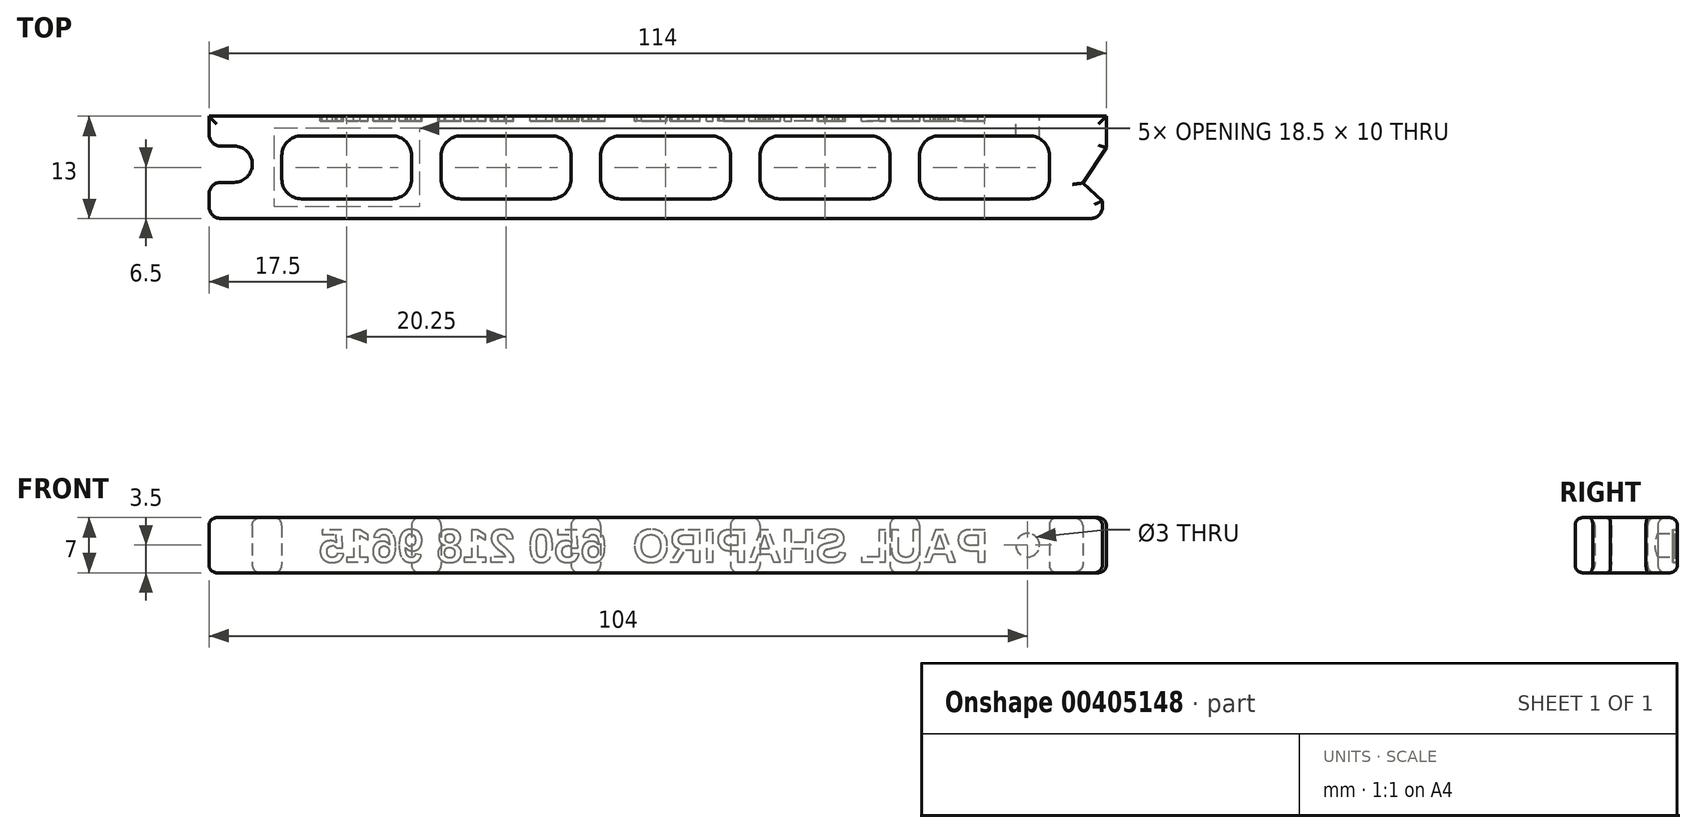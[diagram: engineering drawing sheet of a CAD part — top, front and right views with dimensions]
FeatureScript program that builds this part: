
annotation { "Feature Type Name" : "Feature", "Feature Type Description" : "" }
export const myFeature = defineFeature(function(context is Context, id is Id, definition is map)
    precondition{}
    {
        {
            var Q0;
            Q0=qCreatedBy(makeId("Top.planeOp"),FACE);
            var sketch = newSketch(context, id + "F0", { "sketchPlane" : qUnion([Q0])});
            skLineSegment(sketch, "E0.bottom", {"start": v(1.5, 0) * mm, "end": v(112, 0) * mm});
            skLineSegment(sketch, "E0.top", {"start": v(0, 13) * mm, "end": v(114, 13) * mm});
            skLineSegment(sketch, "E1", {"start": v(0, 13) * mm, "end": v(0, 10.7) * mm});
            skLineSegment(sketch, "E2.bottom", {"start": v(1.5, 4.6) * mm, "end": v(3.2, 4.6) * mm});
            skLineSegment(sketch, "E2.top", {"start": v(1.5, 9.2) * mm, "end": v(3.2, 9.2) * mm});
            skArc(sketch, "E3", {"start": v(3.2, 4.6) * mm, "mid": v(5.5, 6.9) * mm, "end": v(3.2, 9.2) * mm});
            skLineSegment(sketch, "E4.trimOffspring", {"start": v(0, 3.1) * mm, "end": v(0, 1.5) * mm});
            skLineSegment(sketch, "E5", {"start": v(0, 9.2) * mm, "end": v(0, 4.6) * mm, "construction": true});
            skLineSegment(sketch, "E6", {"start": v(0, 6.9) * mm, "end": v(3.2, 6.9) * mm, "construction": true});
            skLineSegment(sketch, "E7", {"start": v(114, 13) * mm, "end": v(114, 9) * mm});
            skPoint(sketch, "E8.visualSharp", {"position": v(0, 0) * mm});
            skArc(sketch, "E8.filletArc", {"start": v(0, 1.5) * mm, "mid": v(0.44, 0.44) * mm, "end": v(1.5, 0) * mm});
            skPoint(sketch, "E9.visualSharp", {"position": v(0, 4.6) * mm});
            skArc(sketch, "E9.filletArc", {"start": v(1.5, 4.6) * mm, "mid": v(0.44, 4.16) * mm, "end": v(0, 3.1) * mm});
            skPoint(sketch, "E10.visualSharp", {"position": v(0, 9.2) * mm});
            skArc(sketch, "E10.filletArc", {"start": v(0, 10.7) * mm, "mid": v(0.44, 9.64) * mm, "end": v(1.5, 9.2) * mm});
            skPoint(sketch, "E11.visualSharp", {"position": v(114, 4.5) * mm});
            skLineSegment(sketch, "E12", {"start": v(114, 4.5) * mm, "end": v(111, 4.5) * mm, "construction": true});
            skLineSegment(sketch, "E13", {"start": v(114, 9) * mm, "end": v(111, 4.5) * mm});
            skLineSegment(sketch, "E14", {"start": v(113.5, 2.25) * mm, "end": v(111, 4.5) * mm});
            skArc(sketch, "E15", {"start": v(112, 0) * mm, "mid": v(113.06, 0.44) * mm, "end": v(113.5, 1.5) * mm});
            skLineSegment(sketch, "E16", {"start": v(112, 1.5) * mm, "end": v(114.8, 1.5) * mm, "construction": true});
            skLineSegment(sketch, "E17", {"start": v(113.5, 2.25) * mm, "end": v(113.5, 1.5) * mm});
            skSolve(sketch);
        }
        {
            var Q0;
            Q0=makeQuery(id+"F0.imprint","IMPRINT",FACE,{"disambiguationData":[TD([[makeQuery(id+"F0.imprint","IMPRINT",EDGE,{"derivedFrom":sQuery(id+"F0.wireOp",EDGE,"E0.bottom")}),1.0]])]});
            extrude(context, id + "F1", {"entities" : qUnion([Q0]), "depth" : 7 * mm});
        }
        {
            var Q0;
            Q0=makeQuery(id+"F1.opExtrude","CAP_FACE",FACE,{"disambiguationData":[OSD([sQuery(id+"F0.wireOp",EDGE,"E0.bottom"),sQuery(id+"F0.wireOp",EDGE,"E0.top"),sQuery(id+"F0.wireOp",EDGE,"E1"),sQuery(id+"F0.wireOp",EDGE,"E2.bottom"),sQuery(id+"F0.wireOp",EDGE,"E2.top"),sQuery(id+"F0.wireOp",EDGE,"E3"),sQuery(id+"F0.wireOp",EDGE,"E4.trimOffspring"),sQuery(id+"F0.wireOp",EDGE,"E7"),sQuery(id+"F0.wireOp",EDGE,"c30ca287-96d4-4dfe-8688-3bdeec023004"),sQuery(id+"F0.wireOp",EDGE,"f645941c-dc99-4dda-a8e2-c4b280260802"),sQuery(id+"F0.wireOp",EDGE,"a89c6d0d-95b4-4aa5-8d05-a083aa38cfd4")])],"isStart":true});
            var sketch = newSketch(context, id + "F2", { "sketchPlane" : qUnion([Q0])});
            skLineSegment(sketch, "E18.bottom", {"start": v(104.25, -2.5) * mm, "end": v(92.75, -2.5) * mm});
            skLineSegment(sketch, "E18.top", {"start": v(104.25, -10.5) * mm, "end": v(92.75, -10.5) * mm});
            skLineSegment(sketch, "E18.left", {"start": v(106.75, -5) * mm, "end": v(106.75, -8) * mm});
            skLineSegment(sketch, "E18.right", {"start": v(90.25, -5) * mm, "end": v(90.25, -8) * mm});
            skLineSegment(sketch, "E19", {"start": v(106.75, -10.5) * mm, "end": v(106.75, -13) * mm, "construction": true});
            skLineSegment(sketch, "E20", {"start": v(106.75, -2.5) * mm, "end": v(106.75, 0) * mm, "construction": true});
            skPoint(sketch, "E21.visualSharp", {"position": v(90.25, -10.5) * mm});
            skArc(sketch, "E21.filletArc", {"start": v(90.25, -8) * mm, "mid": v(90.98, -9.77) * mm, "end": v(92.75, -10.5) * mm});
            skPoint(sketch, "E22.visualSharp", {"position": v(90.25, -2.5) * mm});
            skArc(sketch, "E22.filletArc", {"start": v(92.75, -2.5) * mm, "mid": v(90.98, -3.23) * mm, "end": v(90.25, -5) * mm});
            skPoint(sketch, "E23.visualSharp", {"position": v(106.75, -2.5) * mm});
            skArc(sketch, "E23.filletArc", {"start": v(106.75, -5) * mm, "mid": v(106.02, -3.23) * mm, "end": v(104.25, -2.5) * mm});
            skPoint(sketch, "E24.visualSharp", {"position": v(106.75, -10.5) * mm});
            skArc(sketch, "E24.filletArc", {"start": v(104.25, -10.5) * mm, "mid": v(106.02, -9.77) * mm, "end": v(106.75, -8) * mm});
            skLineSegment(sketch, "E25.1.0.0", {"start": v(84, -2.5) * mm, "end": v(72.5, -2.5) * mm});
            skPoint(sketch, "E25.1.0.1", {"position": v(86.5, -2.5) * mm});
            skLineSegment(sketch, "E25.1.0.2", {"start": v(84, -10.5) * mm, "end": v(72.5, -10.5) * mm});
            skPoint(sketch, "E25.1.0.3", {"position": v(86.5, -10.5) * mm});
            skLineSegment(sketch, "E25.1.0.4", {"start": v(70, -5) * mm, "end": v(70, -8) * mm});
            skLineSegment(sketch, "E25.1.0.5", {"start": v(86.5, -5) * mm, "end": v(86.5, -8) * mm});
            skPoint(sketch, "E25.1.0.6", {"position": v(70, -2.5) * mm});
            skPoint(sketch, "E25.1.0.7", {"position": v(70, -10.5) * mm});
            skArc(sketch, "E25.1.0.8", {"start": v(72.5, -2.5) * mm, "mid": v(70.73, -3.23) * mm, "end": v(70, -5) * mm});
            skArc(sketch, "E25.1.0.9", {"start": v(70, -8) * mm, "mid": v(70.73, -9.77) * mm, "end": v(72.5, -10.5) * mm});
            skArc(sketch, "E25.1.0.10", {"start": v(86.5, -5) * mm, "mid": v(85.77, -3.23) * mm, "end": v(84, -2.5) * mm});
            skArc(sketch, "E25.1.0.11", {"start": v(84, -10.5) * mm, "mid": v(85.77, -9.77) * mm, "end": v(86.5, -8) * mm});
            skLineSegment(sketch, "E25.2.0.0", {"start": v(63.75, -2.5) * mm, "end": v(52.25, -2.5) * mm});
            skPoint(sketch, "E25.2.0.1", {"position": v(66.25, -2.5) * mm});
            skLineSegment(sketch, "E25.2.0.2", {"start": v(63.75, -10.5) * mm, "end": v(52.25, -10.5) * mm});
            skPoint(sketch, "E25.2.0.3", {"position": v(66.25, -10.5) * mm});
            skLineSegment(sketch, "E25.2.0.4", {"start": v(49.75, -5) * mm, "end": v(49.75, -8) * mm});
            skLineSegment(sketch, "E25.2.0.5", {"start": v(66.25, -5) * mm, "end": v(66.25, -8) * mm});
            skPoint(sketch, "E25.2.0.6", {"position": v(49.75, -2.5) * mm});
            skPoint(sketch, "E25.2.0.7", {"position": v(49.75, -10.5) * mm});
            skArc(sketch, "E25.2.0.8", {"start": v(52.25, -2.5) * mm, "mid": v(50.48, -3.23) * mm, "end": v(49.75, -5) * mm});
            skArc(sketch, "E25.2.0.9", {"start": v(49.75, -8) * mm, "mid": v(50.48, -9.77) * mm, "end": v(52.25, -10.5) * mm});
            skArc(sketch, "E25.2.0.10", {"start": v(66.25, -5) * mm, "mid": v(65.52, -3.23) * mm, "end": v(63.75, -2.5) * mm});
            skArc(sketch, "E25.2.0.11", {"start": v(63.75, -10.5) * mm, "mid": v(65.52, -9.77) * mm, "end": v(66.25, -8) * mm});
            skLineSegment(sketch, "E25.3.0.0", {"start": v(43.5, -2.5) * mm, "end": v(32, -2.5) * mm});
            skPoint(sketch, "E25.3.0.1", {"position": v(46, -2.5) * mm});
            skLineSegment(sketch, "E25.3.0.2", {"start": v(43.5, -10.5) * mm, "end": v(32, -10.5) * mm});
            skPoint(sketch, "E25.3.0.3", {"position": v(46, -10.5) * mm});
            skLineSegment(sketch, "E25.3.0.4", {"start": v(29.5, -5) * mm, "end": v(29.5, -8) * mm});
            skLineSegment(sketch, "E25.3.0.5", {"start": v(46, -5) * mm, "end": v(46, -8) * mm});
            skPoint(sketch, "E25.3.0.6", {"position": v(29.5, -2.5) * mm});
            skPoint(sketch, "E25.3.0.7", {"position": v(29.5, -10.5) * mm});
            skArc(sketch, "E25.3.0.8", {"start": v(32, -2.5) * mm, "mid": v(30.23, -3.23) * mm, "end": v(29.5, -5) * mm});
            skArc(sketch, "E25.3.0.9", {"start": v(29.5, -8) * mm, "mid": v(30.23, -9.77) * mm, "end": v(32, -10.5) * mm});
            skArc(sketch, "E25.3.0.10", {"start": v(46, -5) * mm, "mid": v(45.27, -3.23) * mm, "end": v(43.5, -2.5) * mm});
            skArc(sketch, "E25.3.0.11", {"start": v(43.5, -10.5) * mm, "mid": v(45.27, -9.77) * mm, "end": v(46, -8) * mm});
            skLineSegment(sketch, "E25.4.0.0", {"start": v(23.25, -2.5) * mm, "end": v(11.75, -2.5) * mm});
            skPoint(sketch, "E25.4.0.1", {"position": v(25.75, -2.5) * mm});
            skLineSegment(sketch, "E25.4.0.2", {"start": v(23.25, -10.5) * mm, "end": v(11.75, -10.5) * mm});
            skPoint(sketch, "E25.4.0.3", {"position": v(25.75, -10.5) * mm});
            skLineSegment(sketch, "E25.4.0.4", {"start": v(9.25, -5) * mm, "end": v(9.25, -8) * mm});
            skLineSegment(sketch, "E25.4.0.5", {"start": v(25.75, -5) * mm, "end": v(25.75, -8) * mm});
            skPoint(sketch, "E25.4.0.6", {"position": v(9.25, -2.5) * mm});
            skPoint(sketch, "E25.4.0.7", {"position": v(9.25, -10.5) * mm});
            skArc(sketch, "E25.4.0.8", {"start": v(11.75, -2.5) * mm, "mid": v(9.98, -3.23) * mm, "end": v(9.25, -5) * mm});
            skArc(sketch, "E25.4.0.9", {"start": v(9.25, -8) * mm, "mid": v(9.98, -9.77) * mm, "end": v(11.75, -10.5) * mm});
            skArc(sketch, "E25.4.0.10", {"start": v(25.75, -5) * mm, "mid": v(25.02, -3.23) * mm, "end": v(23.25, -2.5) * mm});
            skArc(sketch, "E25.4.0.11", {"start": v(23.25, -10.5) * mm, "mid": v(25.02, -9.77) * mm, "end": v(25.75, -8) * mm});
            skLineSegment(sketch, "E25.direction1", {"start": v(92.75, -2.5) * mm, "end": v(72.5, -2.5) * mm, "construction": true});
            skSolve(sketch);
        }
        {
            var Q0;
            Q0=qSketchRegion(id+"F2",true);
            extrude(context, id + "F3", {"entities" : qUnion([Q0]), "operationType" : NewBodyOperationType.REMOVE, "endBound" : BoundingType.THROUGH_ALL, "oppositeDirection" : true, "depth" : 13.73 * mm});
        }
        {
            var Q0;
            Q0=makeQuery(id+"F1.opExtrude","CAP_FACE",FACE,{"disambiguationData":[OSD([sQuery(id+"F0.wireOp",EDGE,"E0.bottom"),sQuery(id+"F0.wireOp",EDGE,"E0.top"),sQuery(id+"F0.wireOp",EDGE,"E1"),sQuery(id+"F0.wireOp",EDGE,"E2.bottom"),sQuery(id+"F0.wireOp",EDGE,"E2.top"),sQuery(id+"F0.wireOp",EDGE,"E3"),sQuery(id+"F0.wireOp",EDGE,"E4.trimOffspring"),sQuery(id+"F0.wireOp",EDGE,"E7"),sQuery(id+"F0.wireOp",EDGE,"a89c6d0d-95b4-4aa5-8d05-a083aa38cfd4"),sQuery(id+"F0.wireOp",EDGE,"843786d9-8344-4bf4-b63c-bd20b21d23d6.filletArc"),sQuery(id+"F0.wireOp",EDGE,"E8.filletArc"),sQuery(id+"F0.wireOp",EDGE,"E9.filletArc"),sQuery(id+"F0.wireOp",EDGE,"E10.filletArc"),sQuery(id+"F0.wireOp",EDGE,"E13"),sQuery(id+"F0.wireOp",EDGE,"34148787-0765-4789-8ede-2cb2b04cca70")])],"isStart":true});
            var Q1;
            Q1=makeQuery(id+"F1.opExtrude","CAP_FACE",FACE,{"disambiguationData":[OSD([sQuery(id+"F0.wireOp",EDGE,"E0.bottom"),sQuery(id+"F0.wireOp",EDGE,"E0.top"),sQuery(id+"F0.wireOp",EDGE,"E1"),sQuery(id+"F0.wireOp",EDGE,"E2.bottom"),sQuery(id+"F0.wireOp",EDGE,"E2.top"),sQuery(id+"F0.wireOp",EDGE,"E3"),sQuery(id+"F0.wireOp",EDGE,"E4.trimOffspring"),sQuery(id+"F0.wireOp",EDGE,"E7"),sQuery(id+"F0.wireOp",EDGE,"a89c6d0d-95b4-4aa5-8d05-a083aa38cfd4"),sQuery(id+"F0.wireOp",EDGE,"843786d9-8344-4bf4-b63c-bd20b21d23d6.filletArc"),sQuery(id+"F0.wireOp",EDGE,"E8.filletArc"),sQuery(id+"F0.wireOp",EDGE,"E9.filletArc"),sQuery(id+"F0.wireOp",EDGE,"E10.filletArc"),sQuery(id+"F0.wireOp",EDGE,"E13"),sQuery(id+"F0.wireOp",EDGE,"34148787-0765-4789-8ede-2cb2b04cca70")])],"isStart":false});
            fillet(context, id + "F4", {"entities" : qUnion([Q0, Q1]), "radius" : 1 * mm, "allowEdgeOverflow" : false});
        }
        {
            var Q0;
            Q0=makeQuery(id+"F1.opExtrude","SWEPT_FACE",FACE,{"disambiguationData":[OSD([sQuery(id+"F0.wireOp",EDGE,"E0.top")])]});
            var sketch = newSketch(context, id + "F5", { "sketchPlane" : qUnion([Q0])});
            skLineSegment(sketch, "E26", {"start": v(-104, 1) * mm, "end": v(-104, 6) * mm, "construction": true});
            skCircle(sketch, "E27", {"center": v(-104, 3.5) * mm, "radius": 1.5 * mm});
            skSolve(sketch);
        }
        {
            var Q0;
            Q0=makeQuery(id+"F5.imprint","IMPRINT",FACE,{"disambiguationData":[TD([[makeQuery(id+"F5.imprint","IMPRINT",EDGE,{"derivedFrom":sQuery(id+"F5.wireOp",EDGE,"E27")}),1.0]])]});
            extrude(context, id + "F6", {"entities" : qUnion([Q0]), "operationType" : NewBodyOperationType.REMOVE, "endBound" : BoundingType.UP_TO_NEXT, "oppositeDirection" : true, "depth" : 25 * mm});
        }
        {
            var Q0;
            Q0=makeQuery(id+"F1.opExtrude","SWEPT_FACE",FACE,{"disambiguationData":[OSD([sQuery(id+"F0.wireOp",EDGE,"E0.top")])]});
            var sketch = newSketch(context, id + "F7", { "sketchPlane" : qUnion([Q0])});
            skText(sketch, "E28", { "text": "PAUL SHAPIRO  650 218 9615", "fontName": "Arimo-Bold.ttf"});
            skLineSegment(sketch, "E29", {"start": v(-98.95, 5.65) * mm, "end": v(-98.95, 6) * mm, "construction": true});
            skLineSegment(sketch, "E30", {"start": v(-98.95, 1.35) * mm, "end": v(-98.95, 1) * mm, "construction": true});
            const initialGuessF7  = {"E28": [-0.09895, 0.00135, 1, 0, 0.0043]};
            skSetInitialGuess(sketch, initialGuessF7);
            skSolve(sketch);
        }
        {
            var Q0;
            Q0 = qSketchRegion(id + "F7", true);
            extrude(context, id + "F8", {"entities" : qUnion([Q0]), "operationType" : NewBodyOperationType.REMOVE, "oppositeDirection" : true, "depth" : .6 * mm});
        }
    });
